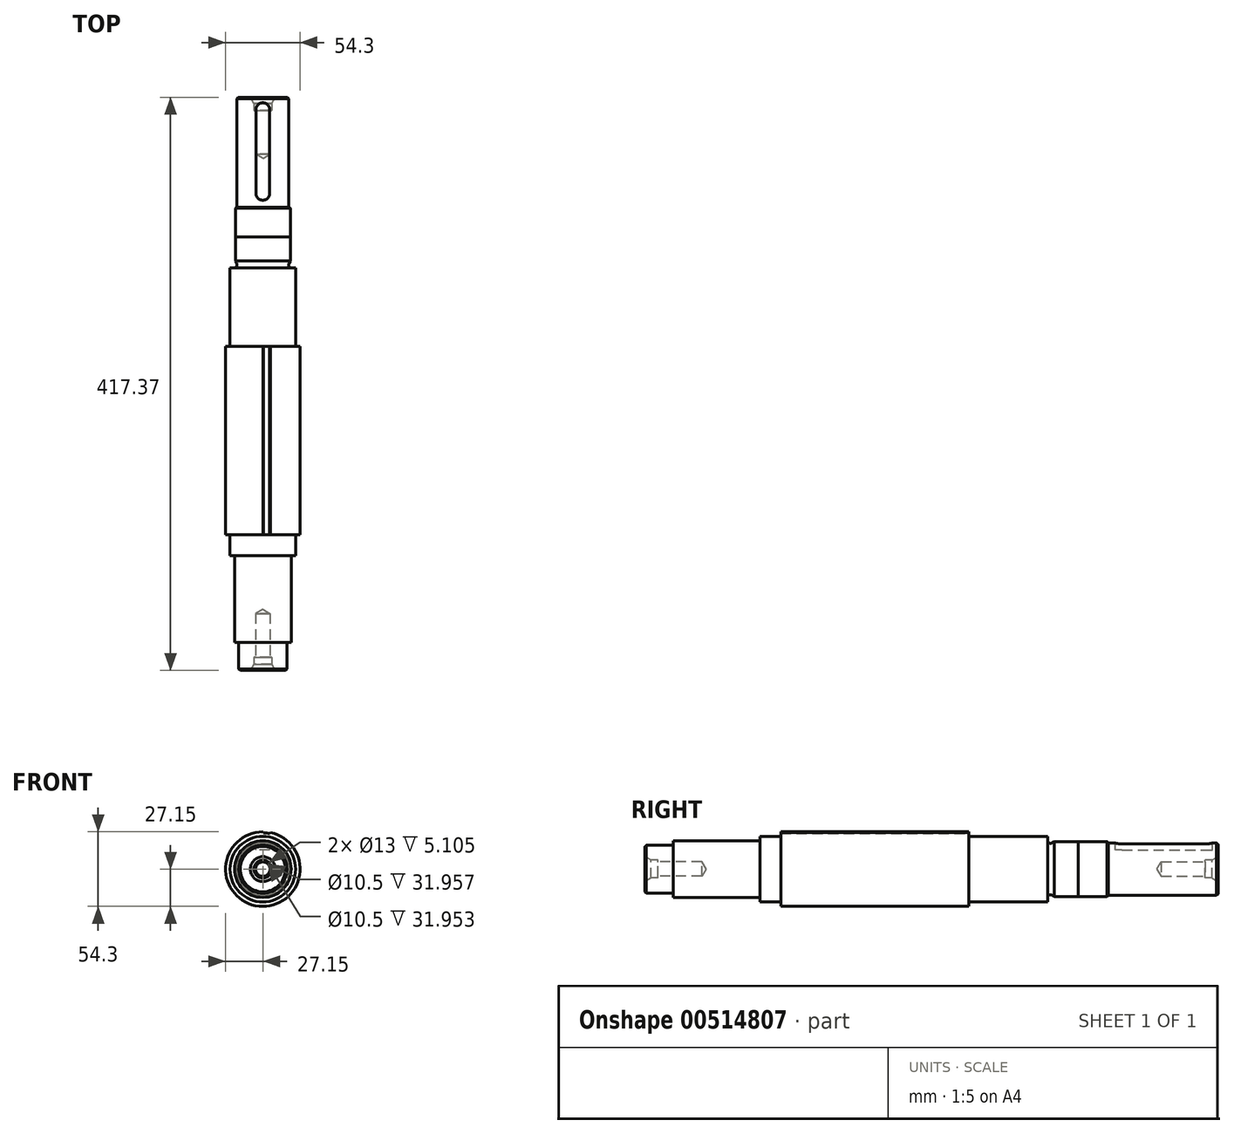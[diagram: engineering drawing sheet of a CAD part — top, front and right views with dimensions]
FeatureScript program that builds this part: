
annotation { "Feature Type Name" : "Feature", "Feature Type Description" : "" }
export const myFeature = defineFeature(function(context is Context, id is Id, definition is map)
    precondition{}
    {
        {
            var Q0;
            Q0=qCreatedBy(makeId("Right.planeOp"),FACE);
            var sketch = newSketch(context, id + "F0", { "sketchPlane" : qUnion([Q0])});
            skLineSegment(sketch, "E0", {"start": v(89.85, 0) * mm, "end": v(-136.66, 0) * mm, "construction": true});
            skLineSegment(sketch, "E1", {"start": v(2.03, 23.88) * mm, "end": v(59.33, 23.88) * mm});
            skLineSegment(sketch, "E2", {"start": v(59.33, 23.88) * mm, "end": v(59.33, 21) * mm});
            skLineSegment(sketch, "E3", {"start": v(103.5, 19.99) * mm, "end": v(103.5, 19) * mm});
            skLineSegment(sketch, "E4", {"start": v(103.5, 19) * mm, "end": v(183.51, 19) * mm});
            skLineSegment(sketch, "E5", {"start": v(183.51, 19) * mm, "end": v(183.51, 9.06) * mm});
            skLineSegment(sketch, "E6", {"start": v(0, 27.15) * mm, "end": v(-135, 27.15) * mm});
            skLineSegment(sketch, "E7", {"start": v(-135, 27.15) * mm, "end": v(-135, 23.88) * mm});
            skLineSegment(sketch, "E8", {"start": v(-135, 23.88) * mm, "end": v(-150.24, 23.88) * mm});
            skLineSegment(sketch, "E9", {"start": v(-150.24, 23.88) * mm, "end": v(-150.24, 20.64) * mm});
            skLineSegment(sketch, "E10", {"start": v(-150.24, 20.64) * mm, "end": v(-213.39, 20.64) * mm});
            skLineSegment(sketch, "E11", {"start": v(-213.39, 20.64) * mm, "end": v(-213.39, 17.5) * mm});
            skLineSegment(sketch, "E12", {"start": v(-213.39, 17.5) * mm, "end": v(-233.86, 17.5) * mm});
            skLineSegment(sketch, "E13", {"start": v(-224.36, 0) * mm, "end": v(174.01, 0) * mm});
            skLineSegment(sketch, "E14", {"start": v(-233.86, 17.5) * mm, "end": v(-233.86, 9.06) * mm});
            skLineSegment(sketch, "E15", {"start": v(64.32, 20) * mm, "end": v(81.79, 20) * mm});
            skLineSegment(sketch, "E16", {"start": v(81.79, 20) * mm, "end": v(81.79, 19.97) * mm});
            skLineSegment(sketch, "E17", {"start": v(81.79, 19.97) * mm, "end": v(103.5, 19.97) * mm});
            skLineSegment(sketch, "E18", {"start": v(0, 27.15) * mm, "end": v(2.03, 27.15) * mm});
            skLineSegment(sketch, "E19", {"start": v(2.03, 27.15) * mm, "end": v(2.03, 23.88) * mm});
            skPoint(sketch, "E20.orphan", {"position": v(0, 23.88) * mm});
            skLineSegment(sketch, "E21", {"start": v(58.67, 18.76) * mm, "end": v(64.58, 18.76) * mm, "construction": true});
            skLineSegment(sketch, "E22", {"start": v(61.57, 21) * mm, "end": v(61.57, 17.9) * mm, "construction": true});
            skLineSegment(sketch, "E23.0", {"start": v(58.67, 21) * mm, "end": v(64.58, 21) * mm, "construction": true});
            skArc(sketch, "E24", {"start": v(59.33, 21) * mm, "mid": v(60.45, 19.06) * mm, "end": v(62.68, 19.06) * mm});
            skLineSegment(sketch, "E25", {"start": v(61.57, 21) * mm, "end": v(62.68, 19.06) * mm, "construction": true});
            skLineSegment(sketch, "E26", {"start": v(62.68, 19.06) * mm, "end": v(64.32, 20) * mm});
            skLineSegment(sketch, "E27.trimOffspring", {"start": v(59.33, 20) * mm, "end": v(59.33, 19.99) * mm});
            skLineSegment(sketch, "E28", {"start": v(174.01, 6.5) * mm, "end": v(179.12, 6.5) * mm});
            skLineSegment(sketch, "E29", {"start": v(179.12, 6.5) * mm, "end": v(183.51, 9.06) * mm});
            skLineSegment(sketch, "E30", {"start": v(174.01, 0) * mm, "end": v(174.01, 6.5) * mm});
            skLineSegment(sketch, "E31", {"start": v(-224.36, 0) * mm, "end": v(-224.36, 6.5) * mm});
            skLineSegment(sketch, "E32", {"start": v(-224.36, 6.5) * mm, "end": v(-229.47, 6.5) * mm});
            skLineSegment(sketch, "E33", {"start": v(-229.47, 6.5) * mm, "end": v(-233.86, 9.06) * mm});
            skPoint(sketch, "E34.orphan", {"position": v(-233.86, 0) * mm});
            skSolve(sketch);
        }
        {
            var Q0;
            Q0=makeQuery(id+"F0.imprint","IMPRINT",FACE,{"disambiguationData":[TD([[makeQuery(id+"F0.imprint","IMPRINT",EDGE,{"derivedFrom":sQuery(id+"F0.wireOp",EDGE,"E1")}),-1.0]])]});
            var Q1;
            Q1=sQuery(id+"F0.wireOp",EDGE,"E13");
            revolve(context, id + "F1", {"entities" : qUnion([Q0]), "axis" : qUnion([Q1]), "revolveType" : RevolveType.FULL});
        }
        {
            var Q0;
            Q0=makeQuery(id+"F1.opRevolve","SWEPT_FACE",FACE,{"disambiguationData":[OSD([sQuery(id+"F0.wireOp",EDGE,"E19")])]});
            var sketch = newSketch(context, id + "F2", { "sketchPlane" : qUnion([Q0])});
            skLineSegment(sketch, "E35", {"start": v(0, 28.92) * mm, "end": v(0, 0) * mm, "construction": true});
            skLineSegment(sketch, "E36", {"start": v(0, 0) * mm, "end": v(-6.07, 28.55) * mm, "construction": true});
            skLineSegment(sketch, "E37", {"start": v(0, 0) * mm, "end": v(-2.96, 28.14) * mm, "construction": true});
            skLineSegment(sketch, "E38", {"start": v(0, 27.15) * mm, "end": v(-0.44, 26.39) * mm});
            skCircle(sketch, "E39", {"center": v(0, 0) * mm, "radius": 26.4 * mm, "construction": true});
            skLineSegment(sketch, "E40.MirrorCS", {"start": v(-5.65, 26.56) * mm, "end": v(-5.05, 25.9) * mm});
            skArc(sketch, "E41", {"start": v(-0.44, 26.39) * mm, "mid": v(-2.76, 26.25) * mm, "end": v(-5.05, 25.9) * mm});
            skSolve(sketch);
        }
        {
            var Q0;
            {var subQ0=sQuery(id+"F2.wireOp",EDGE,"E38");Q0=makeQuery(id+"F2.imprint","IMPRINT",FACE,{"disambiguationData":[TD([[makeQuery(id+"F2.imprint","IMPRINT",EDGE,{"derivedFrom":subQ0}),-1.0]])]});}
            extrude(context, id + "F3", {"entities" : qUnion([Q0]), "operationType" : NewBodyOperationType.REMOVE, "endBound" : BoundingType.THROUGH_ALL, "oppositeDirection" : true, "depth" : 25.4 * mm, "offsetDistance" : 25.4 * mm});
        }
        {
            var Q0;
            Q0=qCreatedBy(makeId("Top.planeOp"),FACE);
            cPlane(context, id + "F4", {"entities" : qUnion([Q0]), "cplaneType" : CPlaneType.OFFSET, "offset" : 19 * mm, "width" : 152.4 * mm, "height" : 152.4 * mm});
        }
        {
            var Q0;
            Q0=qCreatedBy(id+"F4.planeOp",FACE);
            var sketch = newSketch(context, id + "F5", { "sketchPlane" : qUnion([Q0])});
            skLineSegment(sketch, "E42", {"start": v(0, 182.27) * mm, "end": v(0, 95.54) * mm, "construction": true});
            skLineSegment(sketch, "E43", {"start": v(-5, 113.56) * mm, "end": v(-5, 174.52) * mm});
            skLineSegment(sketch, "E44.MirrorCS", {"start": v(5, 113.56) * mm, "end": v(5, 174.52) * mm});
            skArc(sketch, "E45", {"start": v(5, 174.52) * mm, "mid": v(0, 179.52) * mm, "end": v(-5, 174.52) * mm});
            skArc(sketch, "E46", {"start": v(-5, 113.56) * mm, "mid": v(0, 108.56) * mm, "end": v(5, 113.56) * mm});
            skSolve(sketch);
        }
        {
            var Q0;
            Q0=makeQuery(id+"F5.imprint","IMPRINT",FACE,{"disambiguationData":[TD([[makeQuery(id+"F5.imprint","IMPRINT",EDGE,{"derivedFrom":sQuery(id+"F5.wireOp",EDGE,"E43")}),-1.0]])]});
            extrude(context, id + "F6", {"entities" : qUnion([Q0]), "operationType" : NewBodyOperationType.REMOVE, "oppositeDirection" : true, "depth" : 5 * mm, "offsetDistance" : 25.4 * mm});
        }
        {
            var Q0;
            Q0=makeQuery(id+"F1.opRevolve","SWEPT_EDGE",EDGE,{"disambiguationData":[OSD([sQuery(id+"F0.wireOp",EDGE,"E4"),sQuery(id+"F0.wireOp",EDGE,"E5")])]});
            var Q1;
            Q1=makeQuery(id+"F1.opRevolve","SWEPT_EDGE",EDGE,{"disambiguationData":[OSD([sQuery(id+"F0.wireOp",EDGE,"E12"),sQuery(id+"F0.wireOp",EDGE,"E14")])]});
            chamfer(context, id + "F7", {"entities" : qUnion([Q0, Q1]), "width" : 1.02 * mm, "tangentPropagation" : true});
        }
        {
            var Q0;
            Q0=makeQuery(id+"F1.opRevolve","SWEPT_FACE",FACE,{"disambiguationData":[OSD([sQuery(id+"F0.wireOp",EDGE,"HRCa3h44-0kpW-iMQD-Uorv-Gi3B2eKKjRbi")])]});
            var Q1;
            Q1=makeQuery(id+"F1.opRevolve","SWEPT_FACE",FACE,{"disambiguationData":[OSD([sQuery(id+"F0.wireOp",EDGE,"E5")])]});
            cPlane(context, id + "F8", {"entities" : qUnion([Q0, Q1]), "cplaneType" : CPlaneType.OFFSET, "offset" : 9.5 * mm, "oppositeDirection" : true, "width" : 152.4 * mm, "height" : 152.4 * mm});
        }
        {
            var Q0;
            Q0=qCreatedBy(id+"F8.planeOp",FACE);
            var sketch = newSketch(context, id + "F9", { "sketchPlane" : qUnion([Q0])});
            skPoint(sketch, "E47", {"position": v(0, 0) * mm});
            skSolve(sketch);
        }
        {
            var Q0;
            Q0=sQuery(id+"F9.wireOp",VERTEX,"E47");
            var Q1;
            Q1=makeQuery(id+"F1.opRevolve","SWEPT_BODY",BODY,{"disambiguationData":[OSD([sQuery(id+"F0.wireOp",EDGE,"E1"),sQuery(id+"F0.wireOp",EDGE,"E2"),sQuery(id+"F0.wireOp",EDGE,"E3"),sQuery(id+"F0.wireOp",EDGE,"E4"),sQuery(id+"F0.wireOp",EDGE,"E5"),sQuery(id+"F0.wireOp",EDGE,"E6"),sQuery(id+"F0.wireOp",EDGE,"E7"),sQuery(id+"F0.wireOp",EDGE,"E8"),sQuery(id+"F0.wireOp",EDGE,"E9"),sQuery(id+"F0.wireOp",EDGE,"E10"),sQuery(id+"F0.wireOp",EDGE,"E11"),sQuery(id+"F0.wireOp",EDGE,"E12"),sQuery(id+"F0.wireOp",EDGE,"E13"),sQuery(id+"F0.wireOp",EDGE,"E14"),sQuery(id+"F0.wireOp",EDGE,"ZPFujpel-3Slv-UfXd-E2vm-P8XU1JdUdvaP"),sQuery(id+"F0.wireOp",EDGE,"hlsBpjYi-l8cY-SCuO-ZmwT-k2ZF2aup8pd9"),sQuery(id+"F0.wireOp",EDGE,"mw6AryJR-smPn-5KJJ-Pf6F-aFRG8hkgGxIV"),sQuery(id+"F0.wireOp",EDGE,"7sgh2HTh-zS2p-zWoC-WHyA-voJ3dozqxAE8"),sQuery(id+"F0.wireOp",EDGE,"hWQc1cTy-5Q7O-RdFF-MfxO-mkUzDVzf27vZ"),sQuery(id+"F0.wireOp",EDGE,"meQMMjbK-LwDA-AVjP-Z1gU-bTEZ0W9i4j8O"),sQuery(id+"F0.wireOp",EDGE,"m8LHENmK-2iDv-guv8-21Vb-cYcbZqsD0NaV"),sQuery(id+"F0.wireOp",EDGE,"SH7U9YRR-7Q4f-lBVB-PY04-tQoNochQr7GA"),sQuery(id+"F0.wireOp",EDGE,"EdPqvYVC-Fphj-Fu5r-73tG-klrvfsmyz4SQ"),sQuery(id+"F0.wireOp",EDGE,"E15"),sQuery(id+"F0.wireOp",EDGE,"E16"),sQuery(id+"F0.wireOp",EDGE,"E17"),sQuery(id+"F0.wireOp",EDGE,"E18"),sQuery(id+"F0.wireOp",EDGE,"E19"),sQuery(id+"F0.wireOp",EDGE,"E24"),sQuery(id+"F0.wireOp",EDGE,"E26"),sQuery(id+"F0.wireOp",EDGE,"E28"),sQuery(id+"F0.wireOp",EDGE,"E29"),sQuery(id+"F0.wireOp",EDGE,"HRCa3h44-0kpW-iMQD-Uorv-Gi3B2eKKjRbi")])]});
            hole(context, id + "F10", {"style" : HoleStyle.SIMPLE, "endStyle" : HoleEndStyle.BLIND, "standardTappedOrClearance" : lookupTablePath({ "standard" : "ISO", "engagement" : "75%", "pitch" : "1.5 mm", "size" : "M12", "type" : "Tapped" }), "standardBlindInLast" : lookupTablePath({ "standard" : "ISO", "engagement" : "75%", "pitch" : "1.5 mm", "size" : "M12", "type" : "Tapped" }), "holeDiameter" : 10.5 * mm, "showTappedDepth" : true, "holeDepth" : 31.96 * mm, "isTappedThrough" : true, "tappedDepth" : 27.46 * mm, "tapClearance" : 3, "startFromSketch" : true, "locations" : qUnion([Q0]), "scope" : qUnion([Q1]), "majorDiameter" : 12 * mm});
        }
        {
            var Q0;
            Q0=makeQuery(id+"F1.opRevolve","SWEPT_EDGE",EDGE,{"disambiguationData":[OSD([sQuery(id+"F0.wireOp",EDGE,"E3"),sQuery(id+"F0.wireOp",EDGE,"E17")])]});
            chamfer(context, id + "F11", {"entities" : qUnion([Q0]), "width" : 0.76 * mm, "tangentPropagation" : true});
        }
        {
            var Q0;
            Q0=makeQuery(id+"F1.opRevolve","SWEPT_FACE",FACE,{"disambiguationData":[OSD([sQuery(id+"F0.wireOp",EDGE,"E14")])]});
            cPlane(context, id + "F12", {"entities" : qUnion([Q0]), "cplaneType" : CPlaneType.OFFSET, "offset" : 9.5 * mm, "oppositeDirection" : true, "width" : 152.4 * mm, "height" : 152.4 * mm});
        }
        {
            var Q0;
            Q0=qCreatedBy(id+"F12.planeOp",FACE);
            var sketch = newSketch(context, id + "F13", { "sketchPlane" : qUnion([Q0])});
            skPoint(sketch, "E48", {"position": v(0, 0) * mm});
            skSolve(sketch);
        }
        {
            var Q0;
            Q0=sQuery(id+"F13.wireOp",VERTEX,"E48");
            var Q1;
            Q1=makeQuery(id+"F1.opRevolve","SWEPT_BODY",BODY,{"disambiguationData":[OSD([sQuery(id+"F0.wireOp",EDGE,"E1"),sQuery(id+"F0.wireOp",EDGE,"E2"),sQuery(id+"F0.wireOp",EDGE,"E3"),sQuery(id+"F0.wireOp",EDGE,"E4"),sQuery(id+"F0.wireOp",EDGE,"E5"),sQuery(id+"F0.wireOp",EDGE,"E6"),sQuery(id+"F0.wireOp",EDGE,"E7"),sQuery(id+"F0.wireOp",EDGE,"E8"),sQuery(id+"F0.wireOp",EDGE,"E9"),sQuery(id+"F0.wireOp",EDGE,"E10"),sQuery(id+"F0.wireOp",EDGE,"E11"),sQuery(id+"F0.wireOp",EDGE,"E12"),sQuery(id+"F0.wireOp",EDGE,"E13"),sQuery(id+"F0.wireOp",EDGE,"E14"),sQuery(id+"F0.wireOp",EDGE,"E15"),sQuery(id+"F0.wireOp",EDGE,"E16"),sQuery(id+"F0.wireOp",EDGE,"E17"),sQuery(id+"F0.wireOp",EDGE,"E18"),sQuery(id+"F0.wireOp",EDGE,"E19"),sQuery(id+"F0.wireOp",EDGE,"E24"),sQuery(id+"F0.wireOp",EDGE,"E26"),sQuery(id+"F0.wireOp",EDGE,"E28"),sQuery(id+"F0.wireOp",EDGE,"E29"),sQuery(id+"F0.wireOp",EDGE,"E30"),sQuery(id+"F0.wireOp",EDGE,"E31"),sQuery(id+"F0.wireOp",EDGE,"E32"),sQuery(id+"F0.wireOp",EDGE,"E33")])]});
            hole(context, id + "F14", {"style" : HoleStyle.SIMPLE, "endStyle" : HoleEndStyle.BLIND, "standardTappedOrClearance" : lookupTablePath({ "standard" : "ISO", "engagement" : "75%", "pitch" : "1.5 mm", "size" : "M12", "type" : "Tapped" }), "standardBlindInLast" : lookupTablePath({ "standard" : "ISO", "engagement" : "75%", "pitch" : "1.5 mm", "size" : "M12", "type" : "Tapped" }), "holeDiameter" : 10.5 * mm, "showTappedDepth" : true, "holeDepth" : 31.95 * mm, "isTappedThrough" : true, "tappedDepth" : 27.45 * mm, "tapClearance" : 3, "startFromSketch" : true, "locations" : qUnion([Q0]), "scope" : qUnion([Q1]), "majorDiameter" : 12 * mm});
        }
    });
